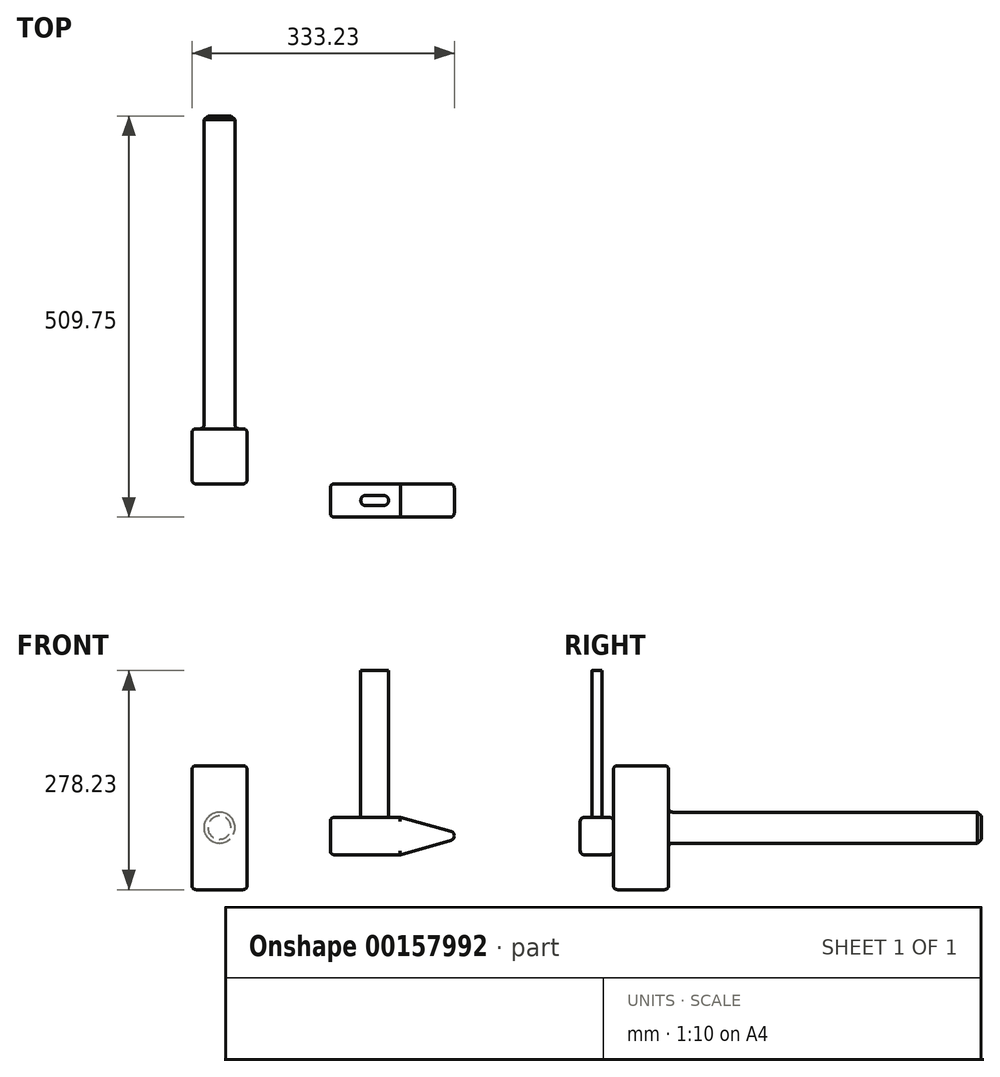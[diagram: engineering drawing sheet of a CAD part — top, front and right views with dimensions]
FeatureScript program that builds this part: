
annotation { "Feature Type Name" : "Feature", "Feature Type Description" : "" }
export const myFeature = defineFeature(function(context is Context, id is Id, definition is map)
    precondition{}
    {
        {
            var Q0;
            Q0=qCreatedBy(makeId("Top.planeOp"),FACE);
            var sketch = newSketch(context, id + "F0", { "sketchPlane" : qUnion([Q0])});
            skLineSegment(sketch, "E0.bottom", {"start": v(0, 0) * mm, "end": v(-70, 0) * mm});
            skLineSegment(sketch, "E0.top", {"start": v(0, 70) * mm, "end": v(-70, 70) * mm});
            skLineSegment(sketch, "E0.left", {"start": v(0, 0) * mm, "end": v(0, 70) * mm});
            skLineSegment(sketch, "E0.right", {"start": v(-70, 0) * mm, "end": v(-70, 70) * mm});
            skSolve(sketch);
        }
        {
            var Q0;
            Q0=makeQuery(id+"F0.imprint","IMPRINT",FACE,{"disambiguationData":[TD([[makeQuery(id+"F0.imprint","IMPRINT",EDGE,{"derivedFrom":sQuery(id+"F0.wireOp",EDGE,"E0.bottom")}),-1.0]])]});
            extrude(context, id + "F1", {"entities" : qUnion([Q0]), "depth" : 157.5 * mm});
        }
        {
            var Q0;
            Q0=makeQuery(id+"F1.opExtrude","SWEPT_FACE",FACE,{"disambiguationData":[OSD([sQuery(id+"F0.wireOp",EDGE,"E0.top")])]});
            var sketch = newSketch(context, id + "F2", { "sketchPlane" : qUnion([Q0])});
            skCircle(sketch, "E1", {"center": v(35, 78.75) * mm, "radius": 19.69 * mm});
            skLineSegment(sketch, "E2", {"start": v(35, 157.5) * mm, "end": v(35, 0) * mm, "construction": true});
            skLineSegment(sketch, "E3", {"start": v(0, 78.75) * mm, "end": v(70, 78.75) * mm, "construction": true});
            skSolve(sketch);
        }
        {
            var Q0;
            Q0=makeQuery(id+"F2.imprint","IMPRINT",FACE,{"disambiguationData":[TD([[makeQuery(id+"F2.imprint","IMPRINT",EDGE,{"derivedFrom":sQuery(id+"F2.wireOp",EDGE,"E1")}),1.0]])]});
            extrude(context, id + "F3", {"entities" : qUnion([Q0]), "operationType" : NewBodyOperationType.ADD, "depth" : 397.5 * mm});
        }
        {
            var Q0;
            Q0=makeQuery(id+"F1.opExtrude","CAP_EDGE",EDGE,{"disambiguationData":[OSD([sQuery(id+"F0.wireOp",EDGE,"E0.bottom")])],"isStart":false});
            var Q1;
            Q1=makeQuery(id+"F1.opExtrude","CAP_EDGE",EDGE,{"disambiguationData":[OSD([sQuery(id+"F0.wireOp",EDGE,"E0.right")])],"isStart":false});
            var Q2;
            Q2=makeQuery(id+"F1.opExtrude","CAP_EDGE",EDGE,{"disambiguationData":[OSD([sQuery(id+"F0.wireOp",EDGE,"E0.top")])],"isStart":false});
            var Q3;
            Q3=makeQuery(id+"F1.opExtrude","CAP_EDGE",EDGE,{"disambiguationData":[OSD([sQuery(id+"F0.wireOp",EDGE,"E0.left")])],"isStart":false});
            var Q4;
            Q4=makeQuery(id+"F1.opExtrude","SWEPT_FACE",FACE,{"disambiguationData":[OSD([sQuery(id+"F0.wireOp",EDGE,"E0.right")])]});
            var Q5;
            Q5=makeQuery(id+"F1.opExtrude","SWEPT_FACE",FACE,{"disambiguationData":[OSD([sQuery(id+"F0.wireOp",EDGE,"E0.bottom")])]});
            var Q6;
            Q6=makeQuery(id+"F1.opExtrude","SWEPT_FACE",FACE,{"disambiguationData":[OSD([sQuery(id+"F0.wireOp",EDGE,"E0.left")])]});
            var Q7;
            Q7=makeQuery(id+"F1.opExtrude","SWEPT_FACE",FACE,{"disambiguationData":[OSD([sQuery(id+"F0.wireOp",EDGE,"E0.top")])]});
            var Q8;
            Q8=makeQuery(id+"F1.opExtrude","CAP_FACE",FACE,{"disambiguationData":[OSD([sQuery(id+"F0.wireOp",EDGE,"E0.bottom"),sQuery(id+"F0.wireOp",EDGE,"E0.top"),sQuery(id+"F0.wireOp",EDGE,"E0.left"),sQuery(id+"F0.wireOp",EDGE,"E0.right")])],"isStart":true});
            fillet(context, id + "F4", {"entities" : qUnion([Q0, Q1, Q2, Q3, Q4, Q5, Q6, Q7, Q8]), "radius" : 5 * mm, "tangentPropagation" : true, "allowEdgeOverflow" : false});
        }
        {
            var Q0;
            Q0=makeQuery(id+"F3.opExtrude","CAP_EDGE",EDGE,{"disambiguationData":[OSD([sQuery(id+"F2.wireOp",EDGE,"E1")])],"isStart":false});
            chamfer(context, id + "F5", {"entities" : qUnion([Q0]), "width" : 5 * mm, "tangentPropagation" : true});
        }
        {
            var Q0;
            Q0=qCreatedBy(makeId("Front.planeOp"),FACE);
            var sketch = newSketch(context, id + "F6", { "sketchPlane" : qUnion([Q0])});
            skLineSegment(sketch, "E4", {"start": v(105.79, 91.73) * mm, "end": v(194.97, 91.73) * mm});
            skLineSegment(sketch, "E5", {"start": v(194.97, 91.73) * mm, "end": v(258.83, 74.15) * mm});
            skLineSegment(sketch, "E6", {"start": v(258.88, 62.6) * mm, "end": v(194.97, 44.3) * mm});
            skLineSegment(sketch, "E7", {"start": v(194.97, 44.3) * mm, "end": v(105.79, 44.3) * mm});
            skLineSegment(sketch, "E8", {"start": v(105.79, 44.3) * mm, "end": v(105.79, 91.73) * mm});
            skPoint(sketch, "E9.visualSharp", {"position": v(279.41, 68.48) * mm});
            skArc(sketch, "E9.filletArc", {"start": v(278.8, 68.3) * mm, "mid": v(278.92, 68.48) * mm, "end": v(278.8, 68.65) * mm});
            skArc(sketch, "E10.filletArc", {"start": v(258.88, 62.6) * mm, "mid": v(263.23, 68.4) * mm, "end": v(258.83, 74.15) * mm});
            skSolve(sketch);
        }
        {
            var Q0;
            Q0=makeQuery(id+"F6.imprint","IMPRINT",FACE,{"disambiguationData":[TD([[makeQuery(id+"F6.imprint","IMPRINT",EDGE,{"derivedFrom":sQuery(id+"F6.wireOp",EDGE,"E4")}),-1.0]])]});
            extrude(context, id + "F7", {"entities" : qUnion([Q0]), "depth" : 42.25 * mm});
        }
        {
            var Q0;
            Q0=makeQuery(id+"F7.opExtrude","CAP_FACE",FACE,{"disambiguationData":[OSD([sQuery(id+"F6.wireOp",EDGE,"E4"),sQuery(id+"F6.wireOp",EDGE,"E5"),sQuery(id+"F6.wireOp",EDGE,"E6"),sQuery(id+"F6.wireOp",EDGE,"E7"),sQuery(id+"F6.wireOp",EDGE,"E8"),sQuery(id+"F6.wireOp",EDGE,"E10.filletArc")])],"isStart":false});
            var Q1;
            Q1=makeQuery(id+"F7.opExtrude","CAP_FACE",FACE,{"disambiguationData":[OSD([sQuery(id+"F6.wireOp",EDGE,"E4"),sQuery(id+"F6.wireOp",EDGE,"E5"),sQuery(id+"F6.wireOp",EDGE,"E6"),sQuery(id+"F6.wireOp",EDGE,"E7"),sQuery(id+"F6.wireOp",EDGE,"E8"),sQuery(id+"F6.wireOp",EDGE,"E10.filletArc")])],"isStart":true});
            var Q2;
            Q2=makeQuery(id+"F7.opExtrude","SWEPT_FACE",FACE,{"disambiguationData":[OSD([sQuery(id+"F6.wireOp",EDGE,"E8")])]});
            fillet(context, id + "F8", {"entities" : qUnion([Q0, Q1, Q2]), "radius" : 5 * mm, "tangentPropagation" : true, "allowEdgeOverflow" : false});
        }
        {
            var Q0;
            Q0=makeQuery(id+"F7.opExtrude","SWEPT_FACE",FACE,{"disambiguationData":[OSD([sQuery(id+"F6.wireOp",EDGE,"E4")])]});
            var sketch = newSketch(context, id + "F9", { "sketchPlane" : qUnion([Q0])});
            skLineSegment(sketch, "E11", {"start": v(110.79, -21.12) * mm, "end": v(194.97, -21.12) * mm, "construction": true});
            skLineSegment(sketch, "E12", {"start": v(162.13, -37.25) * mm, "end": v(162.13, -5) * mm, "construction": true});
            skLineSegment(sketch, "E13.bottom", {"start": v(150.5, -14.8) * mm, "end": v(173.75, -14.8) * mm});
            skLineSegment(sketch, "E13.top", {"start": v(150.5, -27.45) * mm, "end": v(173.75, -27.45) * mm});
            skLineSegment(sketch, "E13.left", {"start": v(144.5, -20.8) * mm, "end": v(144.5, -21.46) * mm});
            skLineSegment(sketch, "E13.right", {"start": v(179.74, -20.8) * mm, "end": v(179.74, -21.46) * mm});
            skPoint(sketch, "E13.middle", {"position": v(162.13, -21.13) * mm});
            skPoint(sketch, "E14.visualSharp", {"position": v(144.5, -14.8) * mm});
            skArc(sketch, "E14.filletArc", {"start": v(150.5, -14.8) * mm, "mid": v(146.26, -16.56) * mm, "end": v(144.5, -20.8) * mm});
            skPoint(sketch, "E15.visualSharp", {"position": v(144.5, -27.45) * mm});
            skArc(sketch, "E15.filletArc", {"start": v(144.5, -21.46) * mm, "mid": v(146.26, -25.7) * mm, "end": v(150.5, -27.45) * mm});
            skPoint(sketch, "E16.visualSharp", {"position": v(179.74, -27.45) * mm});
            skArc(sketch, "E16.filletArc", {"start": v(173.75, -27.45) * mm, "mid": v(177.99, -25.7) * mm, "end": v(179.74, -21.46) * mm});
            skPoint(sketch, "E17.visualSharp", {"position": v(179.74, -14.8) * mm});
            skArc(sketch, "E17.filletArc", {"start": v(179.74, -20.8) * mm, "mid": v(177.99, -16.56) * mm, "end": v(173.75, -14.8) * mm});
            skArc(sketch, "E18.0", {"start": v(184.5, -20.8) * mm, "mid": v(181.35, -13.2) * mm, "end": v(173.75, -10.05) * mm});
            skLineSegment(sketch, "E18.1", {"start": v(150.5, -10.05) * mm, "end": v(173.75, -10.05) * mm});
            skArc(sketch, "E18.2", {"start": v(150.5, -10.05) * mm, "mid": v(142.9, -13.2) * mm, "end": v(139.76, -20.8) * mm});
            skArc(sketch, "E18.3", {"start": v(173.75, -32.2) * mm, "mid": v(181.35, -29.05) * mm, "end": v(184.5, -21.46) * mm});
            skLineSegment(sketch, "E18.4", {"start": v(150.5, -32.2) * mm, "end": v(173.75, -32.2) * mm});
            skArc(sketch, "E18.5", {"start": v(139.76, -21.46) * mm, "mid": v(142.9, -29.05) * mm, "end": v(150.5, -32.2) * mm});
            skLineSegment(sketch, "E18.6", {"start": v(139.76, -20.8) * mm, "end": v(139.76, -21.46) * mm});
            skSolve(sketch);
        }
        {
            var Q0;
            Q0=makeQuery(id+"F9.imprint","IMPRINT",FACE,{"disambiguationData":[TD([[makeQuery(id+"F9.imprint","IMPRINT",EDGE,{"derivedFrom":sQuery(id+"F9.wireOp",EDGE,"E13.bottom")}),-1.0]])]});
            extrude(context, id + "F10", {"entities" : qUnion([Q0]), "operationType" : NewBodyOperationType.ADD, "depth" : 186.5 * mm});
        }
    });
